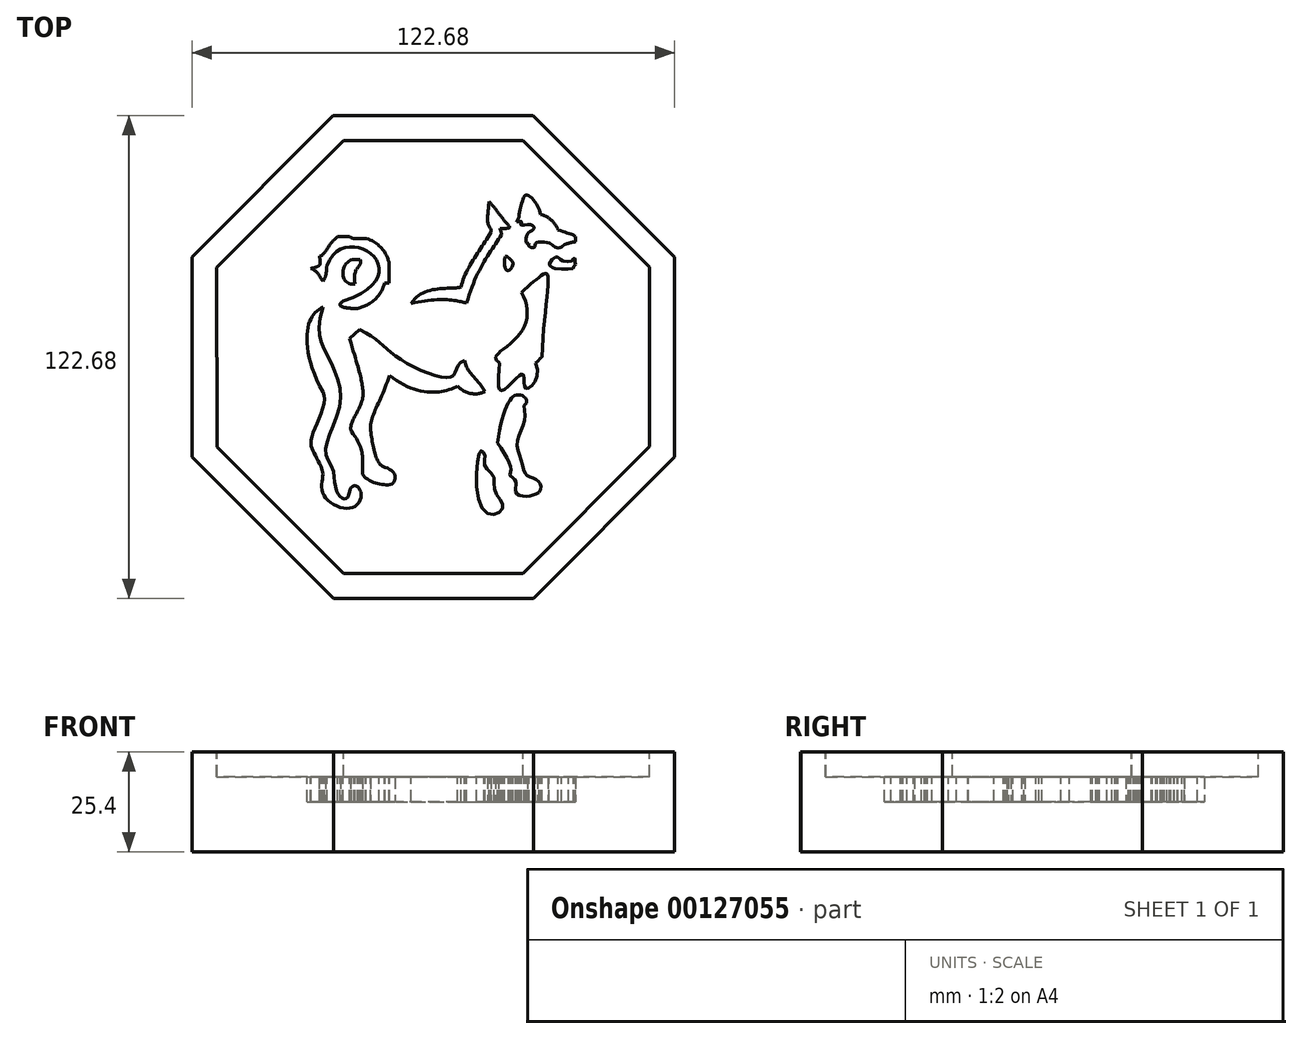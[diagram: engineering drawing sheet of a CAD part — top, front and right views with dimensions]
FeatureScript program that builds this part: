
annotation { "Feature Type Name" : "Feature", "Feature Type Description" : "" }
export const myFeature = defineFeature(function(context is Context, id is Id, definition is map)
    precondition{}
    {
        {
            var Q0;
            Q0=qCreatedBy(makeId("Top.planeOp"),FACE);
            var sketch = newSketch(context, id + "F0", { "sketchPlane" : qUnion([Q0])});
            skCircle(sketch, "E0.cCircle", {"center": v(0, 0) * mm, "radius": 61.32 * mm, "construction": true});
            skLineSegment(sketch, "E0.0", {"start": v(-61.3, -25.44) * mm, "end": v(-61.34, 25.36) * mm});
            skLineSegment(sketch, "E0.1", {"start": v(-61.34, 25.36) * mm, "end": v(-25.44, 61.3) * mm});
            skLineSegment(sketch, "E0.2", {"start": v(-25.44, 61.3) * mm, "end": v(25.36, 61.34) * mm});
            skLineSegment(sketch, "E0.3", {"start": v(25.36, 61.34) * mm, "end": v(61.3, 25.44) * mm});
            skLineSegment(sketch, "E0.4", {"start": v(61.3, 25.44) * mm, "end": v(61.34, -25.36) * mm});
            skLineSegment(sketch, "E0.5", {"start": v(61.34, -25.36) * mm, "end": v(25.44, -61.3) * mm});
            skLineSegment(sketch, "E0.6", {"start": v(25.44, -61.3) * mm, "end": v(-25.36, -61.34) * mm});
            skLineSegment(sketch, "E0.7", {"start": v(-25.36, -61.34) * mm, "end": v(-61.3, -25.44) * mm});
            skPoint(sketch, "E0.0.midPoint", {"position": v(-61.32, -0.04) * mm});
            skSolve(sketch);
        }
        {
            var Q0;
            Q0 = qSketchRegion(id + "F0", true);
            extrude(context, id + "F1", {"entities" : qUnion([Q0]), "depth" : 25.4 * mm});
        }
        {
            var Q0;
            Q0=makeQuery(id+"F1.opExtrude","CAP_FACE",FACE,{"disambiguationData":[OSD([sQuery(id+"F0.wireOp",EDGE,"E0.0"),sQuery(id+"F0.wireOp",EDGE,"E0.1"),sQuery(id+"F0.wireOp",EDGE,"E0.2"),sQuery(id+"F0.wireOp",EDGE,"E0.3"),sQuery(id+"F0.wireOp",EDGE,"E0.4"),sQuery(id+"F0.wireOp",EDGE,"E0.5"),sQuery(id+"F0.wireOp",EDGE,"E0.6"),sQuery(id+"F0.wireOp",EDGE,"E0.7")])],"isStart":false});
            var sketch = newSketch(context, id + "F2", { "sketchPlane" : qUnion([Q0])});
            skLineSegment(sketch, "E1.0", {"start": v(-54.96, -22.8) * mm, "end": v(-54.99, 22.73) * mm});
            skLineSegment(sketch, "E1.1", {"start": v(-22.73, -54.99) * mm, "end": v(-54.96, -22.8) * mm});
            skLineSegment(sketch, "E1.2", {"start": v(-54.99, 22.73) * mm, "end": v(-22.8, 54.96) * mm});
            skLineSegment(sketch, "E1.3", {"start": v(22.8, -54.96) * mm, "end": v(-22.73, -54.99) * mm});
            skLineSegment(sketch, "E1.4", {"start": v(-22.8, 54.96) * mm, "end": v(22.73, 54.99) * mm});
            skLineSegment(sketch, "E1.5", {"start": v(22.73, 54.99) * mm, "end": v(54.96, 22.8) * mm});
            skLineSegment(sketch, "E1.6", {"start": v(54.96, 22.8) * mm, "end": v(54.99, -22.73) * mm});
            skLineSegment(sketch, "E1.7", {"start": v(54.99, -22.73) * mm, "end": v(22.8, -54.96) * mm});
            skSolve(sketch);
        }
        {
            var Q0;
            Q0 = qSketchRegion(id + "F2", true);
            extrude(context, id + "F3", {"entities" : qUnion([Q0]), "operationType" : NewBodyOperationType.REMOVE, "oppositeDirection" : true, "depth" : 6.35 * mm});
        }
        {
            var Q0;
            Q0=makeQuery(id+"F3.boolean.opBoolean","COPY",FACE,{"derivedFrom":makeQuery(id+"F3.opExtrude","CAP_FACE",FACE,{"disambiguationData":[OSD([sQuery(id+"F2.wireOp",EDGE,"E1.0"),sQuery(id+"F2.wireOp",EDGE,"E1.1"),sQuery(id+"F2.wireOp",EDGE,"E1.2"),sQuery(id+"F2.wireOp",EDGE,"E1.3"),sQuery(id+"F2.wireOp",EDGE,"E1.4"),sQuery(id+"F2.wireOp",EDGE,"E1.5"),sQuery(id+"F2.wireOp",EDGE,"E1.6"),sQuery(id+"F2.wireOp",EDGE,"E1.7")])],"isStart":false})});
            var sketch = newSketch(context, id + "F4", { "sketchPlane" : qUnion([Q0])});
            skFitSpline(sketch, "E2", {"points": [v(-28.04, 19.27) * mm, v(-31.12, 22.52) * mm], "startDerivative": vector(-2.58, 3.17) * mm, "endDerivative": vector(-5.5, 1.75) * mm});
            skFitSpline(sketch, "E3", {"points": [v(-28, 12.76) * mm, v(-27.93, 2.59) * mm, v(-26.72, 0) * mm, v(-23.55, -10.89) * mm, v(-27.4, -23.54) * mm, v(-25.3, -29.14) * mm], "startDerivative": vector(-25.33, -70) * mm, "endDerivative": vector(13.84, -41.25) * mm});
            skFitSpline(sketch, "E4", {"points": [v(-28, 12.76) * mm, v(-31.35, 9.18) * mm, v(-28.06, -8.87) * mm], "startDerivative": vector(-12.96, -8.2) * mm, "endDerivative": vector(20.26, -36.46) * mm});
            skFitSpline(sketch, "E5", {"points": [v(-28.06, -8.87) * mm, v(-30.84, -20.22) * mm, v(-30.28, -24.45) * mm, v(-28.06, -29.67) * mm], "startDerivative": vector(10.78, -17.71) * mm, "endDerivative": vector(4.32, -22.67) * mm});
            skFitSpline(sketch, "E6", {"points": [v(-28.06, -29.67) * mm, v(-28.06, -34.63) * mm, v(-21.94, -38.47) * mm, v(-18.38, -35.69) * mm], "startDerivative": vector(0, -14.85) * mm, "endDerivative": vector(3.32, 16.58) * mm});
            skFitSpline(sketch, "E7", {"points": [v(-18.38, -35.69) * mm, v(-18.7, -33.57) * mm, v(-19.82, -32.68) * mm, v(-21.05, -33.46) * mm, v(-21.83, -35.69) * mm, v(-23.5, -35.69) * mm, v(-25.3, -29.14) * mm], "startDerivative": vector(2.1, 18.99) * mm, "endDerivative": vector(-2.16, 31.54) * mm});
            skFitSpline(sketch, "E8", {"points": [v(-18.7, 6.93) * mm, v(-9.25, 0) * mm, v(4.88, -4.87) * mm, v(7.89, -0.86) * mm], "startDerivative": vector(40.53, -18.13) * mm, "endDerivative": vector(29.85, 8.53) * mm});
            skFitSpline(sketch, "E9", {"points": [v(7.89, -0.86) * mm, v(13.12, -8.76) * mm], "startDerivative": vector(2.67, -11.02) * mm, "endDerivative": vector(5.34, -9.68) * mm});
            skFitSpline(sketch, "E10", {"points": [v(6.22, -7.42) * mm, v(13.12, -8.76) * mm], "startDerivative": vector(6.68, -6.68) * mm, "endDerivative": vector(6, 3) * mm});
            skFitSpline(sketch, "E11", {"points": [v(6.22, -7.42) * mm, v(-11.14, -4.64) * mm], "startDerivative": vector(-11.02, -5.68) * mm, "endDerivative": vector(-21.03, 17.03) * mm});
            skFitSpline(sketch, "E12", {"points": [v(-11.14, -4.64) * mm, v(-15.93, -18.66) * mm], "startDerivative": vector(-5.68, -19.36) * mm, "endDerivative": vector(1, -11.68) * mm});
            skFitSpline(sketch, "E13", {"points": [v(-15.93, -18.66) * mm, v(-12.26, -28.01) * mm], "startDerivative": vector(1.67, -12.35) * mm, "endDerivative": vector(6.68, -0.67) * mm});
            skFitSpline(sketch, "E14", {"points": [v(-12.26, -28.01) * mm, v(-9.92, -29.68) * mm, v(-10.25, -32.02) * mm, v(-12.26, -32.46) * mm, v(-14.7, -32.02) * mm, v(-17.26, -30.68) * mm], "startDerivative": vector(13.52, -4.8) * mm, "endDerivative": vector(-12.45, 8.71) * mm});
            skFitSpline(sketch, "E15", {"points": [v(-17.26, -30.68) * mm, v(-18.26, -29.46) * mm], "startDerivative": vector(-1, 1.22) * mm, "endDerivative": vector(-1, 1.22) * mm});
            skFitSpline(sketch, "E16", {"points": [v(-17.93, -29.87) * mm, v(-20.82, -18.89) * mm], "startDerivative": vector(-1.34, 11.24) * mm, "endDerivative": vector(-12.02, 15.36) * mm});
            skFitSpline(sketch, "E17", {"points": [v(-20.82, -18.89) * mm, v(-17.82, -9.87) * mm], "startDerivative": vector(-2.67, 7.01) * mm, "endDerivative": vector(1.67, 11.35) * mm});
            skFitSpline(sketch, "E18", {"points": [v(-17.82, -9.87) * mm, v(-21.27, 4.76) * mm], "startDerivative": vector(-0.33, 11.35) * mm, "endDerivative": vector(-8.01, 27.2) * mm});
            skFitSpline(sketch, "E19", {"points": [v(-21.27, 4.76) * mm, v(-18.7, 6.93) * mm], "startDerivative": vector(2.56, 2.17) * mm, "endDerivative": vector(2.56, 2.17) * mm});
            skFitSpline(sketch, "E20", {"points": [v(-18.64, 24.7) * mm, v(-19.93, 18.56) * mm], "startDerivative": vector(-16.06, 3.57) * mm, "endDerivative": vector(13.38, 2.38) * mm});
            skFitSpline(sketch, "E21", {"points": [v(-19.93, 18.56) * mm, v(-18.64, 24.7) * mm], "startDerivative": vector(-2.38, 13.98) * mm, "endDerivative": vector(-2.97, 5.35) * mm});
            skFitSpline(sketch, "E22", {"points": [v(-5.6, 13.61) * mm, v(8.5, 13.7) * mm], "startDerivative": vector(21.14, 5.16) * mm, "endDerivative": vector(6.84, -2.08) * mm});
            skFitSpline(sketch, "E23", {"points": [v(-5.6, 13.61) * mm, v(7.04, 17.77) * mm], "startDerivative": vector(8.99, 14.54) * mm, "endDerivative": vector(8.5, 2.1) * mm});
            skFitSpline(sketch, "E24", {"points": [v(8.5, 13.7) * mm, v(17.4, 31.09) * mm], "startDerivative": vector(6.79, 25.08) * mm, "endDerivative": vector(8.7, 13.18) * mm});
            skFitSpline(sketch, "E25", {"points": [v(22.41, 16.4) * mm, v(27.45, 20.72) * mm, v(28.86, 21.16) * mm, v(27.63, 0) * mm], "startDerivative": vector(18.27, 16.42) * mm, "endDerivative": vector(-1.45, -55.38) * mm});
            skFitSpline(sketch, "E26", {"points": [v(27.63, 0) * mm, v(25.95, -1.54) * mm], "startDerivative": vector(-1.85, -1.18) * mm, "endDerivative": vector(-1.85, -1.18) * mm});
            skFitSpline(sketch, "E27", {"points": [v(25.95, -1.54) * mm, v(23.47, -7.9) * mm, v(22.77, -4.36) * mm, v(17.47, -8.51) * mm, v(16.85, -1.54) * mm], "startDerivative": vector(21.59, -39.25) * mm, "endDerivative": vector(3.03, 40.46) * mm});
            skFitSpline(sketch, "E28", {"points": [v(16.85, -1.54) * mm, v(15.88, 0) * mm, v(22.15, 6.06) * mm, v(22.41, 16.4) * mm], "startDerivative": vector(-9.81, 7.84) * mm, "endDerivative": vector(-14.24, 23.52) * mm});
            skFitSpline(sketch, "E29", {"points": [v(13.14, -25) * mm, v(12.3, -23.83) * mm, v(11.67, -24.44) * mm, v(12.25, -38.28) * mm, v(16.43, -39.7) * mm, v(17.66, -37.36) * mm, v(15.65, -34.1) * mm, v(15.23, -30.15) * mm, v(13.03, -27.73) * mm, v(13.14, -25) * mm]});
            skFitSpline(sketch, "E30", {"points": [v(23.11, -12.28) * mm, v(23.73, -11.35) * mm, v(22.98, -10.04) * mm, v(21.2, -9.66) * mm, v(19.52, -10.88) * mm, v(16.34, -21.83) * mm], "startDerivative": vector(6.27, 8.06) * mm, "endDerivative": vector(-4.25, -38.23) * mm});
            skFitSpline(sketch, "E31", {"points": [v(16.34, -21.83) * mm, v(19.7, -28.57) * mm, v(19.52, -30.06) * mm, v(20.92, -31.47) * mm, v(21, -34.37) * mm, v(23.77, -35.39) * mm, v(26.85, -34.36) * mm], "startDerivative": vector(19.62, -30.29) * mm, "endDerivative": vector(17.13, 9.18) * mm});
            skFitSpline(sketch, "E32", {"points": [v(26.85, -34.36) * mm, v(27.32, -32.77) * mm, v(26.67, -31.55) * mm, v(24.98, -30.62) * mm, v(23.4, -29.68) * mm, v(22.36, -26.22) * mm, v(21.32, -21.78) * mm, v(22.92, -17.05) * mm, v(23.11, -12.28) * mm], "startDerivative": vector(13.3, 12.01) * mm, "endDerivative": vector(-3.29, 30.51) * mm});
            skFitSpline(sketch, "E33", {"points": [v(-28.04, 19.27) * mm, v(-27.03, 23.22) * mm], "startDerivative": vector(3.19, 3.11) * mm, "endDerivative": vector(0.5, 1.73) * mm});
            skFitSpline(sketch, "E34", {"points": [v(-27.03, 23.22) * mm, v(-22.91, 14.18) * mm], "startDerivative": vector(13.85, 37) * mm, "endDerivative": vector(-62.1, -20.36) * mm});
            skFitSpline(sketch, "E35", {"points": [v(-22.91, 14.18) * mm, v(-19.19, 12.35) * mm], "startDerivative": vector(-7.34, -4.67) * mm, "endDerivative": vector(7.01, 0.17) * mm});
            skFitSpline(sketch, "E36", {"points": [v(-19.19, 12.35) * mm, v(-12.34, 18.86) * mm], "startDerivative": vector(7.51, 2.34) * mm, "endDerivative": vector(3.84, 13.52) * mm});
            skFitSpline(sketch, "E37", {"points": [v(-12.34, 18.86) * mm, v(-11.23, 18.86) * mm], "startDerivative": vector(1.11, 0) * mm, "endDerivative": vector(1.11, 0) * mm});
            skFitSpline(sketch, "E38", {"points": [v(-11.23, 18.86) * mm, v(-11.23, 23.8) * mm], "startDerivative": vector(0, 4.95) * mm, "endDerivative": vector(0, 4.95) * mm});
            skFitSpline(sketch, "E39", {"points": [v(-11.23, 23.8) * mm, v(-17.02, 30.15) * mm], "startDerivative": vector(-1.17, 6) * mm, "endDerivative": vector(-12.02, 4.17) * mm});
            skFitSpline(sketch, "E40", {"points": [v(-17.02, 30.15) * mm, v(-21.3, 30.6) * mm], "startDerivative": vector(-4.34, 0) * mm, "endDerivative": vector(-3.17, 2.67) * mm});
            skFitSpline(sketch, "E41", {"points": [v(-21.3, 30.6) * mm, v(-24.3, 30.6) * mm], "startDerivative": vector(-3, 0) * mm, "endDerivative": vector(-3, 0) * mm});
            skFitSpline(sketch, "E42", {"points": [v(-24.3, 30.6) * mm, v(-28.87, 25.6) * mm], "startDerivative": vector(-7.01, -4.84) * mm, "endDerivative": vector(-4.34, -0.83) * mm});
            skFitSpline(sketch, "E43", {"points": [v(-28.87, 25.6) * mm, v(-28.87, 23.36) * mm], "startDerivative": vector(0, -2.23) * mm, "endDerivative": vector(-0.83, -2) * mm});
            skFitSpline(sketch, "E44", {"points": [v(-28.87, 23.36) * mm, v(-31.12, 22.52) * mm], "startDerivative": vector(-1.84, -1.67) * mm, "endDerivative": vector(-2.26, -0.4) * mm});
            skFitSpline(sketch, "E45", {"points": [v(7.04, 17.77) * mm, v(14.6, 31.7) * mm], "startDerivative": vector(3.37, 15.11) * mm, "endDerivative": vector(7.57, 13.94) * mm});
            skFitSpline(sketch, "E46", {"points": [v(14.6, 31.7) * mm, v(13.98, 33.67) * mm, v(14.15, 39.49) * mm], "startDerivative": vector(2.2, 6.03) * mm, "endDerivative": vector(0.48, 10.1) * mm});
            skFitSpline(sketch, "E47", {"points": [v(14.15, 39.49) * mm, v(19.17, 33.43) * mm], "startDerivative": vector(5.6, -5.68) * mm, "endDerivative": vector(5.6, -5.68) * mm});
            skFitSpline(sketch, "E48", {"points": [v(16.96, 32.65) * mm, v(18.96, 32.74) * mm, v(19.42, 32.93) * mm, v(19.17, 33.43) * mm], "startDerivative": vector(4.26, -0.5) * mm, "endDerivative": vector(-1.6, 2.14) * mm});
            skFitSpline(sketch, "E49", {"points": [v(16.96, 32.65) * mm, v(17.4, 31.09) * mm], "startDerivative": vector(0.44, -2.01) * mm, "endDerivative": vector(0.44, -2.01) * mm});
            skFitSpline(sketch, "E50", {"points": [v(21.73, 35.55) * mm, v(22.52, 39.24) * mm, v(23.55, 41.17) * mm, v(25.67, 39.61) * mm, v(27.3, 36.15) * mm], "startDerivative": vector(0.33, 16.39) * mm, "endDerivative": vector(3.25, -13.86) * mm});
            skFitSpline(sketch, "E51", {"points": [v(21.73, 35.55) * mm, v(21.14, 34.3) * mm], "startDerivative": vector(-0.6, -1.25) * mm, "endDerivative": vector(-0.6, -1.25) * mm});
            skFitSpline(sketch, "E52", {"points": [v(21.14, 34.3) * mm, v(22.45, 34.3) * mm, v(22.17, 33.65) * mm, v(24.66, 33.61) * mm, v(25.6, 32.77) * mm, v(24.87, 31.96) * mm, v(23.76, 31.03) * mm, v(23.73, 28.96) * mm, v(24.33, 28.9) * mm], "startDerivative": vector(16, 2.66) * mm, "endDerivative": vector(7.99, 2.08) * mm});
            skFitSpline(sketch, "E53", {"points": [v(24.33, 28.9) * mm, v(24.33, 28.1) * mm, v(25.67, 27.9) * mm, v(26.08, 28.9) * mm, v(29.51, 28.9) * mm, v(30.92, 27.9) * mm, v(32.63, 27.97) * mm], "startDerivative": vector(-2.62, -7.53) * mm, "endDerivative": vector(11.21, 6.63) * mm});
            skFitSpline(sketch, "E54", {"points": [v(32.63, 27.97) * mm, v(33.41, 28.6) * mm, v(34.35, 28.9) * mm, v(34.32, 28.9) * mm], "startDerivative": vector(1.3, 1.46) * mm, "endDerivative": vector(-0.6, -0.04) * mm});
            skFitSpline(sketch, "E55", {"points": [v(27.3, 36.15) * mm, v(31.74, 32.28) * mm], "startDerivative": vector(2.83, 0.6) * mm, "endDerivative": vector(2.42, -6.62) * mm});
            skFitSpline(sketch, "E56", {"points": [v(31.74, 32.28) * mm, v(35.39, 31.05) * mm, v(36.16, 30.56) * mm, v(36.16, 30.04) * mm, v(36.05, 29.34) * mm, v(35.32, 29.16) * mm, v(34.35, 28.9) * mm], "startDerivative": vector(13.62, -4.32) * mm, "endDerivative": vector(-6, -2.07) * mm});
            skFitSpline(sketch, "E57", {"points": [v(18.39, 25.55) * mm, v(18.63, 22.01) * mm, v(20.17, 23.2) * mm, v(20.07, 24.25) * mm, v(19.5, 24.88) * mm, v(18.39, 25.55) * mm]});
            skFitSpline(sketch, "E58", {"points": [v(31.04, 25.41) * mm, v(29.4, 23.55) * mm, v(29.57, 23.34) * mm, v(30.1, 22.82) * mm, v(30.8, 22.54) * mm, v(35.53, 22.57) * mm, v(35.6, 22.85) * mm, v(35.88, 23.17) * mm, v(36.12, 23.41) * mm, v(36.02, 24.4) * mm, v(35.98, 25.13) * mm, v(35.5, 24.92) * mm, v(35.21, 24.43) * mm, v(32.65, 24.46) * mm, v(32.02, 25.13) * mm, v(31.67, 25.3) * mm, v(31.04, 25.41) * mm]});
            skSolve(sketch);
        }
        {
            var Q0;
            Q0 = qSketchRegion(id + "F4", true);
            extrude(context, id + "F5", {"entities" : qUnion([Q0]), "operationType" : NewBodyOperationType.REMOVE, "oppositeDirection" : true, "depth" : 6.35 * mm});
        }
    });
